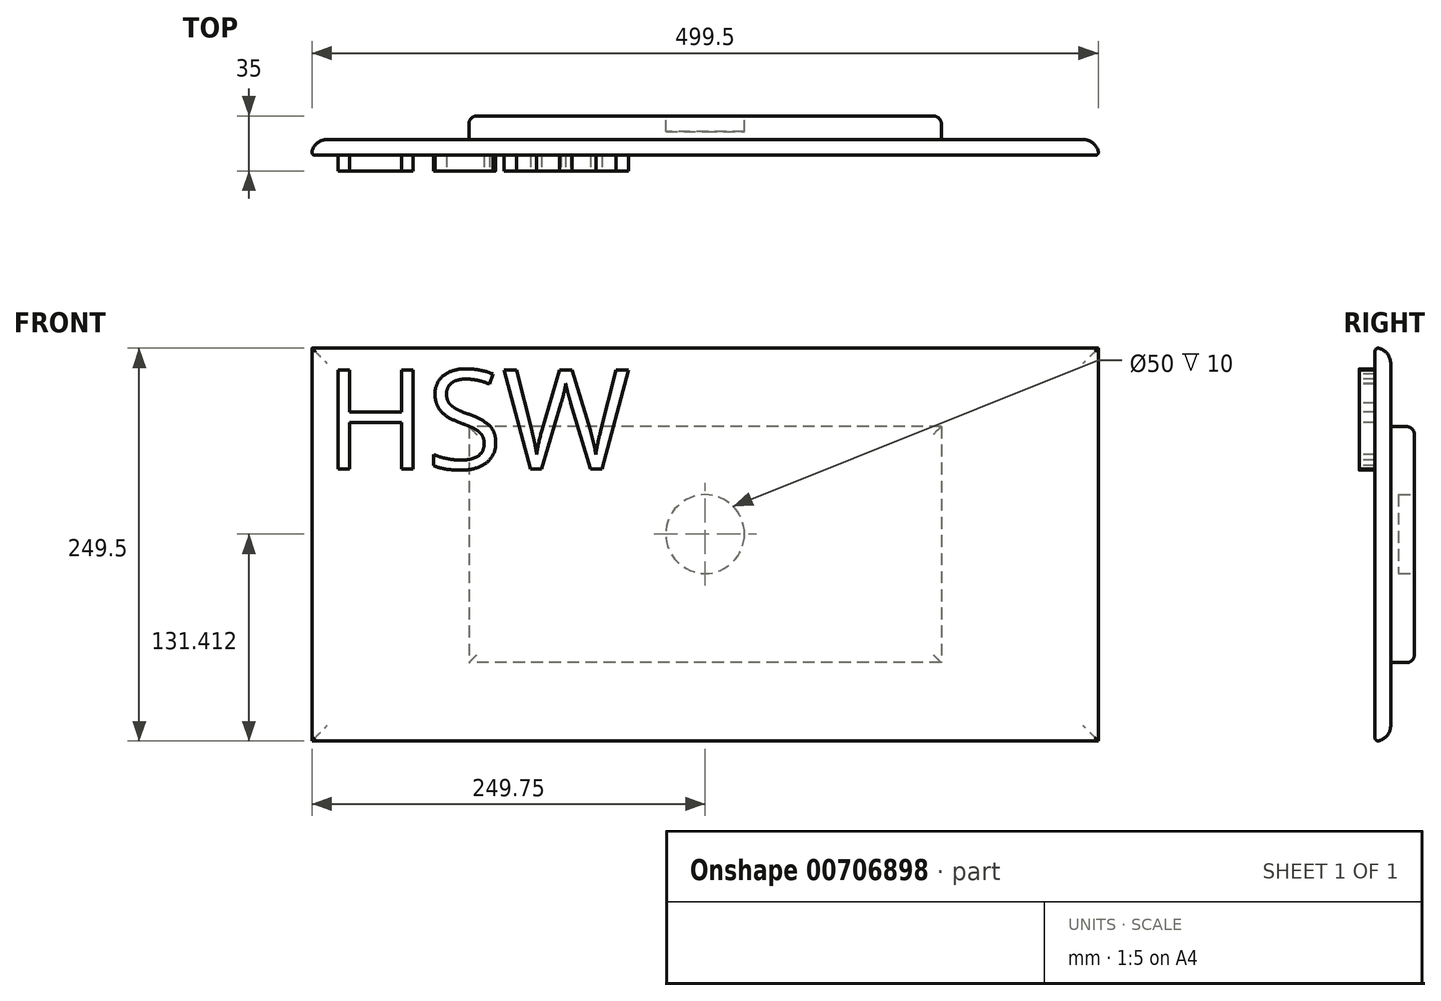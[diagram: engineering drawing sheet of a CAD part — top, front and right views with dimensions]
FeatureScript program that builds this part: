
annotation { "Feature Type Name" : "Feature", "Feature Type Description" : "" }
export const myFeature = defineFeature(function(context is Context, id is Id, definition is map)
    precondition{}
    {
        {
            var Q0;
            Q0=qCreatedBy(makeId("Front.planeOp"),FACE);
            var sketch = newSketch(context, id + "F0", { "sketchPlane" : qUnion([Q0])});
            skLineSegment(sketch, "E0.bottom", {"start": v(-250, 125) * mm, "end": v(250, 125) * mm});
            skLineSegment(sketch, "E0.top", {"start": v(-250, -125) * mm, "end": v(250, -125) * mm});
            skLineSegment(sketch, "E0.left", {"start": v(-250, 125) * mm, "end": v(-250, -125) * mm});
            skLineSegment(sketch, "E0.right", {"start": v(250, 125) * mm, "end": v(250, -125) * mm});
            skSolve(sketch);
        }
        {
            var Q0;
            Q0=makeQuery(id+"F0.imprint","IMPRINT",FACE,{"disambiguationData":[TD([[makeQuery(id+"F0.imprint","IMPRINT",EDGE,{"derivedFrom":sQuery(id+"F0.wireOp",EDGE,"E0.bottom")}),-1.0]])]});
            extrude(context, id + "F1", {"entities" : qUnion([Q0]), "depth" : 10 * mm, "offsetDistance" : 25 * mm});
        }
        {
            var Q0;
            Q0=makeQuery(id+"F1.opExtrude","CAP_FACE",FACE,{"disambiguationData":[OSD([sQuery(id+"F0.wireOp",EDGE,"E0.bottom"),sQuery(id+"F0.wireOp",EDGE,"E0.top"),sQuery(id+"F0.wireOp",EDGE,"E0.left"),sQuery(id+"F0.wireOp",EDGE,"E0.right")])],"isStart":true});
            var sketch = newSketch(context, id + "F2", { "sketchPlane" : qUnion([Q0])});
            skLineSegment(sketch, "E1.bottom", {"start": v(-150, 75) * mm, "end": v(150, 75) * mm});
            skLineSegment(sketch, "E1.top", {"start": v(-150, -75) * mm, "end": v(150, -75) * mm});
            skLineSegment(sketch, "E1.left", {"start": v(-150, 75) * mm, "end": v(-150, -75) * mm});
            skLineSegment(sketch, "E1.right", {"start": v(150, 75) * mm, "end": v(150, -75) * mm});
            skSolve(sketch);
        }
        {
            var Q0;
            Q0 = qSketchRegion(id + "F2", true);
            extrude(context, id + "F3", {"entities" : qUnion([Q0]), "operationType" : NewBodyOperationType.ADD, "depth" : 15 * mm, "offsetDistance" : 25 * mm});
        }
        {
            var Q0;
            Q0=makeQuery(id+"F3.opExtrude","CAP_FACE",FACE,{"disambiguationData":[OSD([sQuery(id+"F2.wireOp",EDGE,"E1.bottom"),sQuery(id+"F2.wireOp",EDGE,"E1.top"),sQuery(id+"F2.wireOp",EDGE,"E1.left"),sQuery(id+"F2.wireOp",EDGE,"E1.right")])],"isStart":false});
            var sketch = newSketch(context, id + "F4", { "sketchPlane" : qUnion([Q0])});
            skCircle(sketch, "E2", {"center": v(0, 6.66) * mm, "radius": 25 * mm});
            skSolve(sketch);
        }
        {
            var Q0;
            Q0=makeQuery(id+"F1.opExtrude","CAP_EDGE",EDGE,{"disambiguationData":[OSD([sQuery(id+"F0.wireOp",EDGE,"E0.bottom")])],"isStart":true});
            var Q1;
            Q1=makeQuery(id+"F1.opExtrude","CAP_EDGE",EDGE,{"disambiguationData":[OSD([sQuery(id+"F0.wireOp",EDGE,"E0.right")])],"isStart":true});
            var Q2;
            Q2=makeQuery(id+"F1.opExtrude","CAP_EDGE",EDGE,{"disambiguationData":[OSD([sQuery(id+"F0.wireOp",EDGE,"E0.left")])],"isStart":true});
            var Q3;
            Q3=makeQuery(id+"F1.opExtrude","CAP_EDGE",EDGE,{"disambiguationData":[OSD([sQuery(id+"F0.wireOp",EDGE,"E0.top")])],"isStart":true});
            var Q4;
            Q4=makeQuery(id+"F3.opExtrude","CAP_EDGE",EDGE,{"disambiguationData":[OSD([sQuery(id+"F2.wireOp",EDGE,"I1KsXPmI-l7sH-km47-Jh46-oBsfdFnX57Ig.bottom")])],"isStart":false});
            var Q5;
            Q5=makeQuery(id+"F3.opExtrude","CAP_EDGE",EDGE,{"disambiguationData":[OSD([sQuery(id+"F2.wireOp",EDGE,"I1KsXPmI-l7sH-km47-Jh46-oBsfdFnX57Ig.left")])],"isStart":false});
            var Q6;
            Q6=makeQuery(id+"F3.opExtrude","CAP_EDGE",EDGE,{"disambiguationData":[OSD([sQuery(id+"F2.wireOp",EDGE,"I1KsXPmI-l7sH-km47-Jh46-oBsfdFnX57Ig.top")])],"isStart":false});
            var Q7;
            Q7=makeQuery(id+"F3.opExtrude","CAP_EDGE",EDGE,{"disambiguationData":[OSD([sQuery(id+"F2.wireOp",EDGE,"I1KsXPmI-l7sH-km47-Jh46-oBsfdFnX57Ig.right")])],"isStart":false});
            fillet(context, id + "F5", {"entities" : qUnion([Q0, Q1, Q2, Q3, Q4, Q5, Q6, Q7]), "radius" : 10 * mm, "tangentPropagation" : true, "allowEdgeOverflow" : false});
        }
        {
            var Q0;
            Q0 = qSketchRegion(id + "F4", true);
            extrude(context, id + "F6", {"entities" : qUnion([Q0]), "operationType" : NewBodyOperationType.REMOVE, "oppositeDirection" : true, "depth" : 10 * mm, "offsetDistance" : 25 * mm});
        }
        {
            var Q0;
            Q0 = qSketchRegion(id + "F4", true);
            extrude(context, id + "F7", {"entities" : qUnion([Q0]), "operationType" : NewBodyOperationType.REMOVE, "endBound" : BoundingType.UP_TO_NEXT, "oppositeDirection" : true, "depth" : 10 * mm, "offsetDistance" : 25 * mm});
        }
        {
            var Q0;
            Q0=qCreatedBy(makeId("Front.planeOp"),FACE);
            cPlane(context, id + "F8", {"entities" : qUnion([Q0]), "cplaneType" : CPlaneType.OFFSET, "offset" : 20 * mm, "width" : 150 * mm, "height" : 150 * mm});
        }
        {
            var Q0;
            Q0=qCreatedBy(id+"F8.planeOp",FACE);
            var sketch = newSketch(context, id + "F9", { "sketchPlane" : qUnion([Q0])});
            skText(sketch, "E3", { "text": "HSW", "fontName": "OpenSans-Regular.ttf"});
            const initialGuessF9  = {"E3": [-0.24165, 0.04813, 1, 0, 0.06316]};
            skSetInitialGuess(sketch, initialGuessF9);
            skSolve(sketch);
        }
        {
            var Q0;
            Q0 = qSketchRegion(id + "F9", true);
            extrude(context, id + "F10", {"entities" : qUnion([Q0]), "endBound" : BoundingType.UP_TO_NEXT, "oppositeDirection" : true, "depth" : 25 * mm, "offsetDistance" : 25 * mm});
        }
        {
            var Q0;
            {var subQ0=sQuery(id+"F0.wireOp",EDGE,"E0.bottom");Q0=makeQuery(id+"F5.opFillet","BLEND_EDGE",EDGE,{"blendedFrom":[makeQuery(id+"F1.opExtrude","CAP_EDGE",EDGE,{"disambiguationData":[OSD([subQ0])],"isStart":true}),makeQuery(id+"F1.opExtrude","CAP_FACE",FACE,{"disambiguationData":[OSD([subQ0,sQuery(id+"F0.wireOp",EDGE,"E0.top"),sQuery(id+"F0.wireOp",EDGE,"E0.left"),sQuery(id+"F0.wireOp",EDGE,"E0.right")])],"isStart":false})],"blendedInto":[makeQuery(id+"F1.opExtrude","CAP_FACE",FACE,{"disambiguationData":[OSD([subQ0,sQuery(id+"F0.wireOp",EDGE,"E0.top"),sQuery(id+"F0.wireOp",EDGE,"E0.left"),sQuery(id+"F0.wireOp",EDGE,"E0.right")])],"isStart":false})]});}
            var Q1;
            {var subQ0=sQuery(id+"F0.wireOp",EDGE,"E0.left");Q1=makeQuery(id+"F5.opFillet","BLEND_EDGE",EDGE,{"blendedFrom":[makeQuery(id+"F1.opExtrude","CAP_EDGE",EDGE,{"disambiguationData":[OSD([subQ0])],"isStart":true}),makeQuery(id+"F1.opExtrude","CAP_FACE",FACE,{"disambiguationData":[OSD([sQuery(id+"F0.wireOp",EDGE,"E0.bottom"),sQuery(id+"F0.wireOp",EDGE,"E0.top"),subQ0,sQuery(id+"F0.wireOp",EDGE,"E0.right")])],"isStart":false})],"blendedInto":[makeQuery(id+"F1.opExtrude","CAP_FACE",FACE,{"disambiguationData":[OSD([sQuery(id+"F0.wireOp",EDGE,"E0.bottom"),sQuery(id+"F0.wireOp",EDGE,"E0.top"),subQ0,sQuery(id+"F0.wireOp",EDGE,"E0.right")])],"isStart":false})]});}
            var Q2;
            {var subQ0=sQuery(id+"F0.wireOp",EDGE,"E0.top");Q2=makeQuery(id+"F5.opFillet","BLEND_EDGE",EDGE,{"blendedFrom":[makeQuery(id+"F1.opExtrude","CAP_EDGE",EDGE,{"disambiguationData":[OSD([subQ0])],"isStart":true}),makeQuery(id+"F1.opExtrude","CAP_FACE",FACE,{"disambiguationData":[OSD([sQuery(id+"F0.wireOp",EDGE,"E0.bottom"),subQ0,sQuery(id+"F0.wireOp",EDGE,"E0.left"),sQuery(id+"F0.wireOp",EDGE,"E0.right")])],"isStart":false})],"blendedInto":[makeQuery(id+"F1.opExtrude","CAP_FACE",FACE,{"disambiguationData":[OSD([sQuery(id+"F0.wireOp",EDGE,"E0.bottom"),subQ0,sQuery(id+"F0.wireOp",EDGE,"E0.left"),sQuery(id+"F0.wireOp",EDGE,"E0.right")])],"isStart":false})]});}
            var Q3;
            {var subQ0=sQuery(id+"F0.wireOp",EDGE,"E0.right");Q3=makeQuery(id+"F5.opFillet","BLEND_EDGE",EDGE,{"blendedFrom":[makeQuery(id+"F1.opExtrude","CAP_EDGE",EDGE,{"disambiguationData":[OSD([subQ0])],"isStart":true}),makeQuery(id+"F1.opExtrude","CAP_FACE",FACE,{"disambiguationData":[OSD([sQuery(id+"F0.wireOp",EDGE,"E0.bottom"),sQuery(id+"F0.wireOp",EDGE,"E0.top"),sQuery(id+"F0.wireOp",EDGE,"E0.left"),subQ0])],"isStart":false})],"blendedInto":[makeQuery(id+"F1.opExtrude","CAP_FACE",FACE,{"disambiguationData":[OSD([sQuery(id+"F0.wireOp",EDGE,"E0.bottom"),sQuery(id+"F0.wireOp",EDGE,"E0.top"),sQuery(id+"F0.wireOp",EDGE,"E0.left"),subQ0])],"isStart":false})]});}
            fillet(context, id + "F11", {"entities" : qUnion([Q0, Q1, Q2, Q3]), "radius" : 2 * mm, "tangentPropagation" : true, "allowEdgeOverflow" : false});
        }
        {
            var Q0;
            Q0=makeQuery(id+"F3.opExtrude","CAP_EDGE",EDGE,{"disambiguationData":[OSD([sQuery(id+"F2.wireOp",EDGE,"E1.bottom")])],"isStart":false});
            var Q1;
            Q1=makeQuery(id+"F3.opExtrude","CAP_EDGE",EDGE,{"disambiguationData":[OSD([sQuery(id+"F2.wireOp",EDGE,"E1.left")])],"isStart":false});
            var Q2;
            Q2=makeQuery(id+"F3.opExtrude","CAP_EDGE",EDGE,{"disambiguationData":[OSD([sQuery(id+"F2.wireOp",EDGE,"E1.top")])],"isStart":false});
            var Q3;
            Q3=makeQuery(id+"F3.opExtrude","CAP_EDGE",EDGE,{"disambiguationData":[OSD([sQuery(id+"F2.wireOp",EDGE,"E1.right")])],"isStart":false});
            var Q4;
            Q4=makeQuery(id+"F3.opExtrude","CAP_EDGE",EDGE,{"disambiguationData":[OSD([sQuery(id+"F2.wireOp",EDGE,"E1.right")])],"isStart":true});
            var Q5;
            Q5=makeQuery(id+"F3.opExtrude","CAP_EDGE",EDGE,{"disambiguationData":[OSD([sQuery(id+"F2.wireOp",EDGE,"E1.bottom")])],"isStart":true});
            var Q6;
            Q6=makeQuery(id+"F3.opExtrude","CAP_EDGE",EDGE,{"disambiguationData":[OSD([sQuery(id+"F2.wireOp",EDGE,"E1.left")])],"isStart":true});
            var Q7;
            Q7=makeQuery(id+"F3.opExtrude","CAP_EDGE",EDGE,{"disambiguationData":[OSD([sQuery(id+"F2.wireOp",EDGE,"E1.top")])],"isStart":true});
            fillet(context, id + "F12", {"entities" : qUnion([Q0, Q1, Q2, Q3, Q4, Q5, Q6, Q7]), "radius" : 5 * mm, "tangentPropagation" : true, "allowEdgeOverflow" : false});
        }
    });
